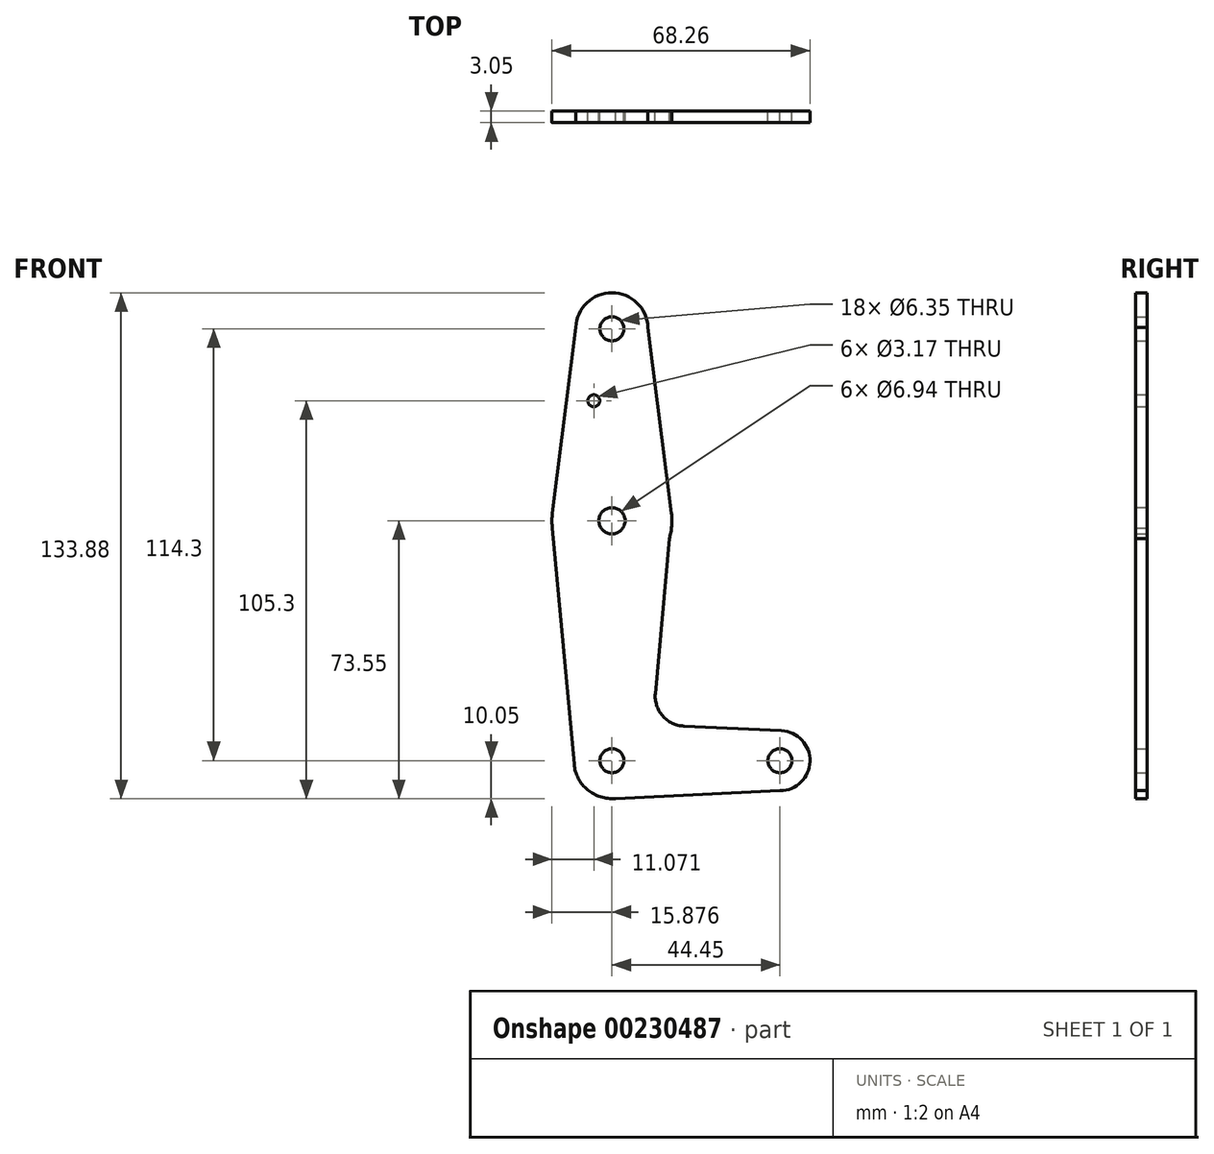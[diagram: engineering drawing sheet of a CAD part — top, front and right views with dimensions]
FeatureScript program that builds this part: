
annotation { "Feature Type Name" : "Feature", "Feature Type Description" : "" }
export const myFeature = defineFeature(function(context is Context, id is Id, definition is map)
    precondition{}
    {
        {
            var Q0;
            Q0=qCreatedBy(makeId("Front.planeOp"),FACE);
            var sketch = newSketch(context, id + "F0", { "sketchPlane" : qUnion([Q0])});
            skLineSegment(sketch, "E0", {"start": v(-9.86, 63.5) * mm, "end": v(-9.86, 0) * mm, "construction": true});
            skLineSegment(sketch, "E1", {"start": v(-9.86, 63.5) * mm, "end": v(-9.86, 114.3) * mm, "construction": true});
            skCircle(sketch, "E2", {"center": v(-9.86, 114.3) * mm, "radius": 9.53 * mm});
            skCircle(sketch, "E3", {"center": v(-9.86, 63.5) * mm, "radius": 15.88 * mm});
            skCircle(sketch, "E4", {"center": v(34.59, 0) * mm, "radius": 7.94 * mm});
            skCircle(sketch, "E5", {"center": v(-9.86, 0) * mm, "radius": 10.05 * mm});
            skLineSegment(sketch, "E6", {"start": v(-9.86, 0) * mm, "end": v(34.59, 0) * mm, "construction": true});
            skLineSegment(sketch, "E7", {"start": v(-19.38, 114.66) * mm, "end": v(-25.61, 65.5) * mm});
            skLineSegment(sketch, "E8", {"start": v(-0.35, 114.66) * mm, "end": v(5.88, 65.5) * mm});
            skLineSegment(sketch, "E9", {"start": v(5.88, 65.5) * mm, "end": v(1.6, 17.8) * mm});
            skLineSegment(sketch, "E10", {"start": v(-25.61, 61.5) * mm, "end": v(-19.87, -0.92) * mm});
            skLineSegment(sketch, "E11", {"start": v(9.14, 9.15) * mm, "end": v(34.96, 7.93) * mm});
            skLineSegment(sketch, "E12", {"start": v(-9.86, -10.05) * mm, "end": v(34.59, -7.94) * mm});
            skArc(sketch, "E13.filletArc", {"start": v(1.6, 17.8) * mm, "mid": v(3.52, 11.87) * mm, "end": v(9.14, 9.15) * mm});
            skCircle(sketch, "E14", {"center": v(-14.67, 95.25) * mm, "radius": 1.59 * mm});
            skCircle(sketch, "E15", {"center": v(-9.86, 114.3) * mm, "radius": 3.18 * mm});
            skCircle(sketch, "E16", {"center": v(-9.86, 63.5) * mm, "radius": 3.47 * mm});
            skCircle(sketch, "E17", {"center": v(-9.86, 0) * mm, "radius": 3.18 * mm});
            skCircle(sketch, "E18", {"center": v(34.59, 0) * mm, "radius": 3.18 * mm});
            skSolve(sketch);
        }
        {
            var Q0;
            Q0 = qSketchRegion(id + "F0", true);
            extrude(context, id + "F1", {"entities" : qUnion([Q0]), "depth" : 3.05 * mm});
        }
    });
